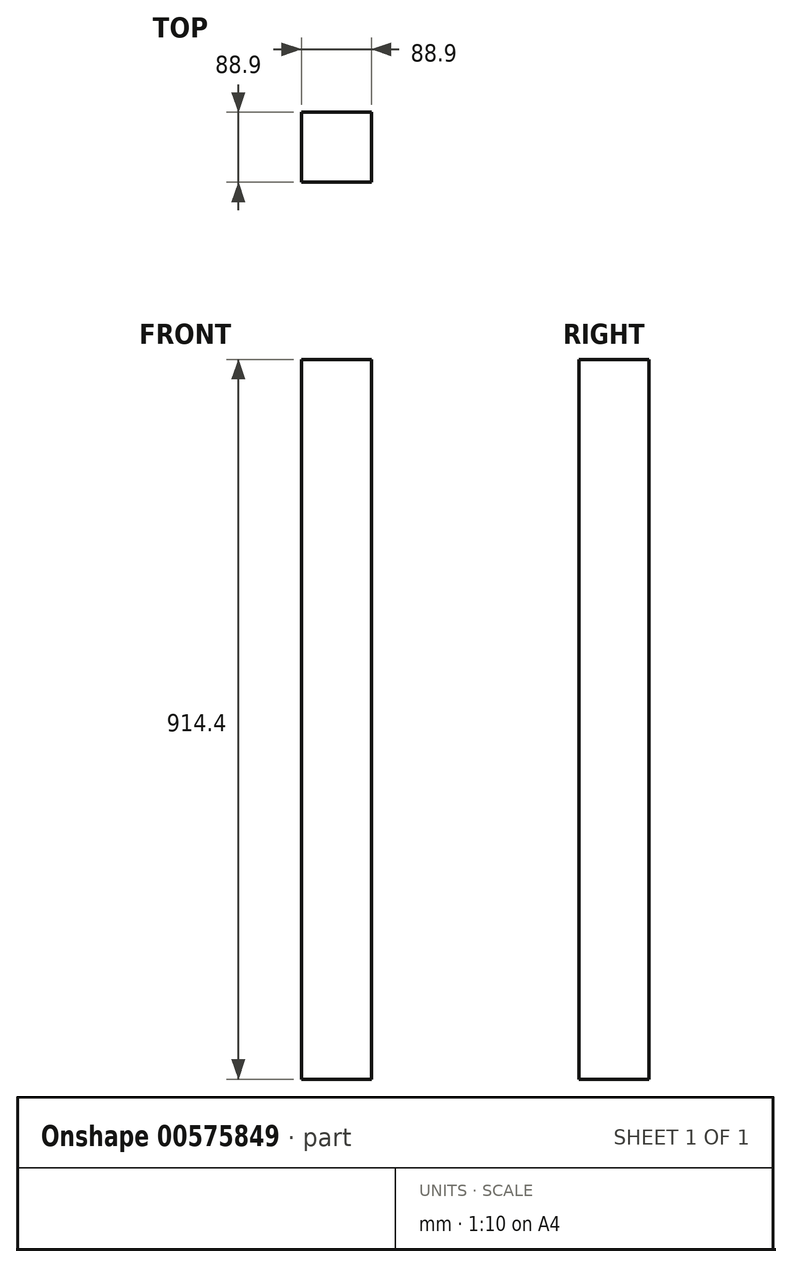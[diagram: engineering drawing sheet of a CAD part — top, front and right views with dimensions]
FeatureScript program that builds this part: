
annotation { "Feature Type Name" : "Feature", "Feature Type Description" : "" }
export const myFeature = defineFeature(function(context is Context, id is Id, definition is map)
    precondition{}
    {
        {
            var Q0;
            Q0=qCreatedBy(makeId("Top.planeOp"),FACE);
            var sketch = newSketch(context, id + "F0", { "sketchPlane" : qUnion([Q0])});
            skLineSegment(sketch, "E0.bottom", {"start": v(0, 0) * mm, "end": v(88.9, 0) * mm});
            skLineSegment(sketch, "E0.top", {"start": v(0, -88.9) * mm, "end": v(88.9, -88.9) * mm});
            skLineSegment(sketch, "E0.left", {"start": v(0, 0) * mm, "end": v(0, -88.9) * mm});
            skLineSegment(sketch, "E0.right", {"start": v(88.9, 0) * mm, "end": v(88.9, -88.9) * mm});
            skSolve(sketch);
        }
        {
            var Q0;
            Q0 = qSketchRegion(id + "F0", true);
            extrude(context, id + "F1", {"entities" : qUnion([Q0]), "depth" : 914.4 * mm, "offsetDistance" : 25.4 * mm});
        }
    });
